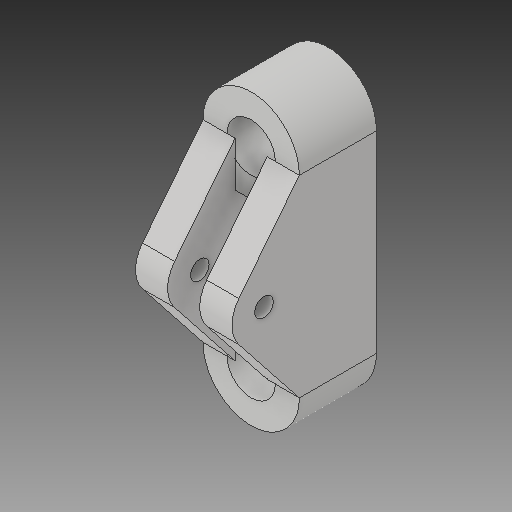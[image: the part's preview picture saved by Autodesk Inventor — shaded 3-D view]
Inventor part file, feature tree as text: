
AUTODESK INVENTOR PART (.ipt)
format: ipt  version: 2017 SP1 (Build 210196100, 196)  size: 166,912 bytes
history: native  units: mm
features: extrude x3, sketch x3, projected_geometry x3, mirror x1
ambient origin geometry x8: Origin, YZ Plane, XZ Plane, XY Plane, X Axis, Y Axis, Z Axis, Center Point
bodies: Solid1 (feature_tree)
feature tree (10):
  extrude  "Extrusion1"  Depth=30.0mm
  extrude  "Extrusion2"  Depth=30.0mm
  extrude  "Extrusion3"  Depth=10.0mm
  mirror  "Mirror1"
  sketch  "Sketch1"  dims[d0=30.0mm d1=6.1mm]
  sketch  "Sketch2"  dims[d2=15.0mm d3=30.0mm]
  projected_geometry  "Projected Loop1"
  sketch  "Sketch3"  dims[d4=24.0mm d5=0.0mm d6=10.0mm d7=32.0mm d8=14.0mm d9=0.0mm d10=25.0mm d11=5.8mm d12=10.0mm d13=14.0mm d14=0.0mm]
  projected_geometry  "Projected Loop2"
  projected_geometry  "Projected Loop3"
